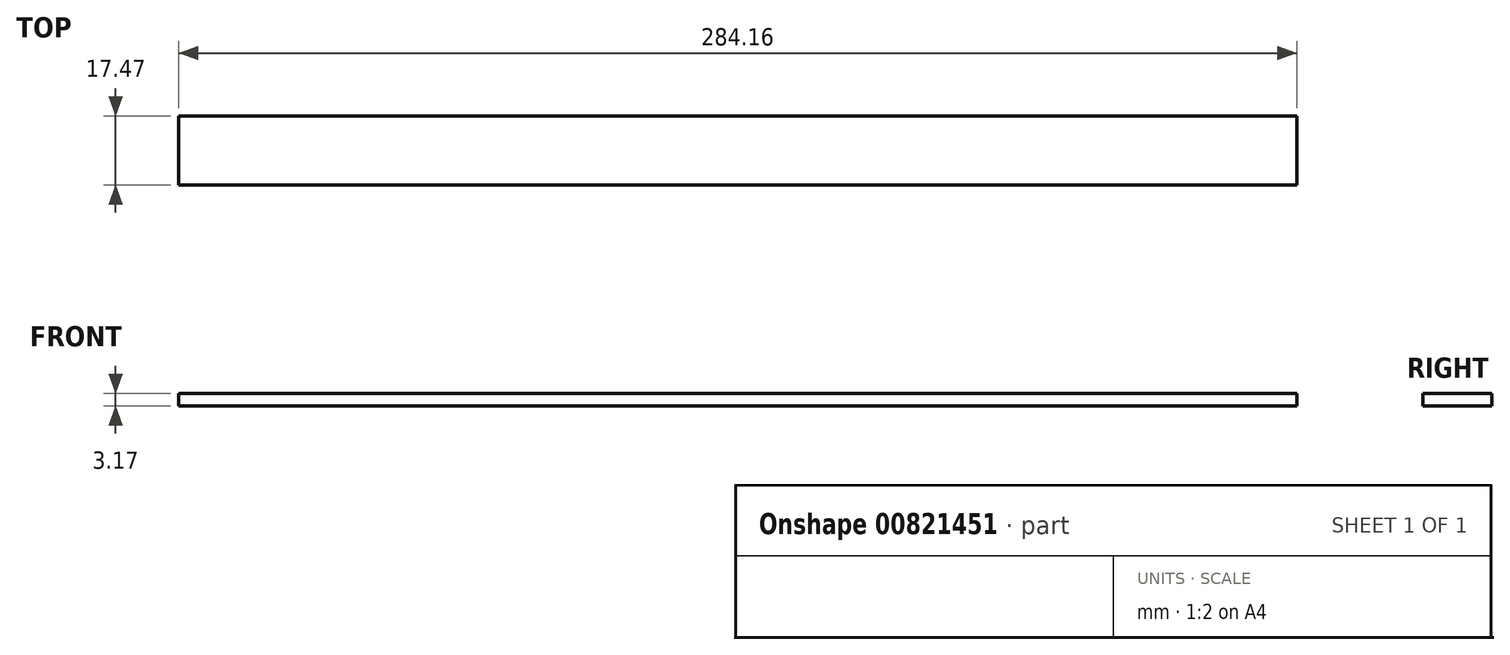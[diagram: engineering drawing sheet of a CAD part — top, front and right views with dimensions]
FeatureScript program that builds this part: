
annotation { "Feature Type Name" : "Feature", "Feature Type Description" : "" }
export const myFeature = defineFeature(function(context is Context, id is Id, definition is map)
    precondition{}
    {
        {
            var Q0;
            Q0=qCreatedBy(makeId("Top.planeOp"),FACE);
            var sketch = newSketch(context, id + "F0", { "sketchPlane" : qUnion([Q0])});
            skLineSegment(sketch, "E0.bottom", {"start": v(-142.08, -11.06) * mm, "end": v(142.08, -11.06) * mm});
            skLineSegment(sketch, "E0.top", {"start": v(-142.08, 6.4) * mm, "end": v(142.08, 6.4) * mm});
            skLineSegment(sketch, "E0.left", {"start": v(-142.08, -11.06) * mm, "end": v(-142.08, 6.4) * mm});
            skLineSegment(sketch, "E0.right", {"start": v(142.08, -11.06) * mm, "end": v(142.08, 6.4) * mm});
            skPoint(sketch, "E0.middle", {"position": v(0, -2.32) * mm});
            skSolve(sketch);
        }
        {
            var Q0;
            Q0 = qSketchRegion(id + "F0", true);
            extrude(context, id + "F1", {"entities" : qUnion([Q0]), "depth" : 3.17 * mm, "offsetDistance" : 25.4 * mm});
        }
    });
